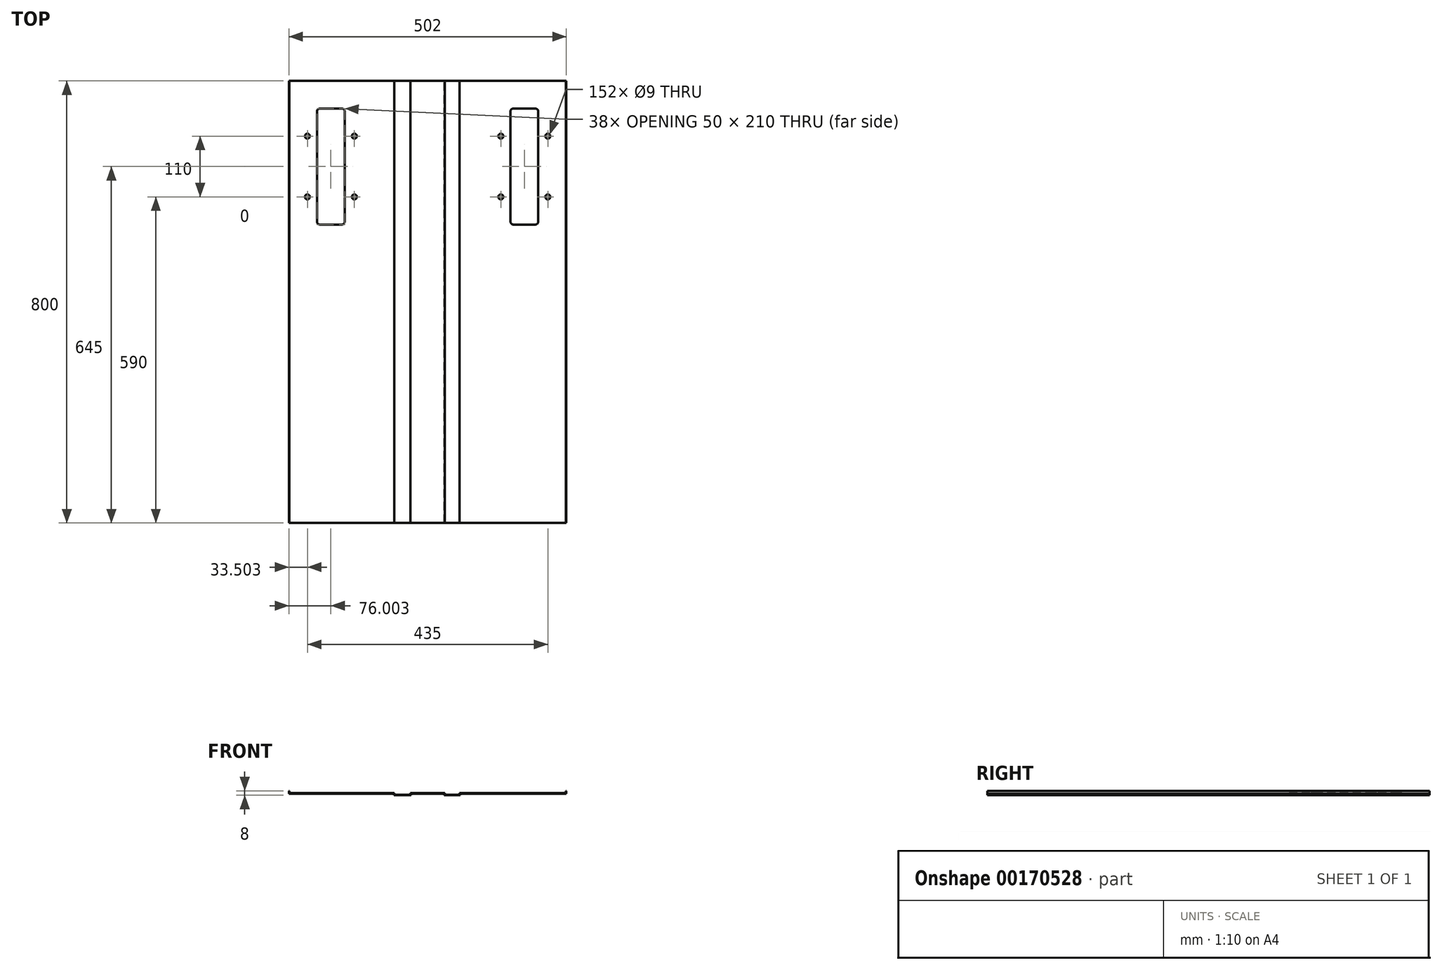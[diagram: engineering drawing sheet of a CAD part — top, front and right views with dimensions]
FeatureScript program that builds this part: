
annotation { "Feature Type Name" : "Feature", "Feature Type Description" : "" }
export const myFeature = defineFeature(function(context is Context, id is Id, definition is map)
    precondition{}
    {
        {
            var Q0;
            Q0=qCreatedBy(makeId("Front.planeOp"),FACE);
            var sketch = newSketch(context, id + "F0", { "sketchPlane" : qUnion([Q0])});
            skLineSegment(sketch, "E0.bottom", {"start": v(-10.98, 0) * mm, "end": v(179.02, 0) * mm});
            skLineSegment(sketch, "E0.top", {"start": v(-9.98, 1) * mm, "end": v(180.02, 1) * mm});
            skLineSegment(sketch, "E0.left", {"start": v(-10.98, 0) * mm, "end": v(-10.98, 1) * mm});
            skLineSegment(sketch, "E0.right", {"start": v(491.02, 0) * mm, "end": v(491.02, 1) * mm});
            skLineSegment(sketch, "E1", {"start": v(240.02, 1) * mm, "end": v(240.02, 44.54) * mm, "construction": true});
            skLineSegment(sketch, "E2.0", {"start": v(179.02, -3) * mm, "end": v(210.02, -3) * mm});
            skLineSegment(sketch, "E3.0", {"start": v(180.02, -2) * mm, "end": v(209.02, -2) * mm});
            skLineSegment(sketch, "E4", {"start": v(210.02, 0) * mm, "end": v(210.02, -3) * mm});
            skLineSegment(sketch, "E5", {"start": v(270.02, 0) * mm, "end": v(270.02, -3) * mm});
            skLineSegment(sketch, "E6.0", {"start": v(180.02, 1) * mm, "end": v(180.02, -2) * mm});
            skLineSegment(sketch, "E7.0", {"start": v(209.02, 1) * mm, "end": v(209.02, -2) * mm});
            skLineSegment(sketch, "E8.0", {"start": v(271.02, 1) * mm, "end": v(271.02, -2) * mm});
            skLineSegment(sketch, "E9.0", {"start": v(298.02, 1) * mm, "end": v(298.02, -2) * mm});
            skLineSegment(sketch, "E10.trimOffspring", {"start": v(271.02, -2) * mm, "end": v(298.02, -2) * mm});
            skLineSegment(sketch, "E11.trimOffspring", {"start": v(270.02, -3) * mm, "end": v(299.02, -3) * mm});
            skLineSegment(sketch, "E12.trimOffspring", {"start": v(179.02, 0) * mm, "end": v(179.02, -3) * mm});
            skLineSegment(sketch, "E13.trimOffspring", {"start": v(210.02, 0) * mm, "end": v(270.02, 0) * mm});
            skLineSegment(sketch, "E14.trimOffspring", {"start": v(209.02, 1) * mm, "end": v(271.02, 1) * mm});
            skPoint(sketch, "E15.orphan", {"position": v(210.02, 16.2) * mm});
            skPoint(sketch, "E16.orphan", {"position": v(270.02, 16.47) * mm});
            skLineSegment(sketch, "E17.trimOffspring", {"start": v(299.02, 0) * mm, "end": v(491.02, 0) * mm});
            skLineSegment(sketch, "E18.trimOffspring", {"start": v(298.02, 1) * mm, "end": v(490.02, 1) * mm});
            skLineSegment(sketch, "E19.trimOffspring", {"start": v(299.02, 0) * mm, "end": v(299.02, -3) * mm});
            skLineSegment(sketch, "E20", {"start": v(-10.98, 1) * mm, "end": v(-10.98, 5) * mm});
            skLineSegment(sketch, "E21", {"start": v(-10.98, 5) * mm, "end": v(-9.98, 5) * mm});
            skLineSegment(sketch, "E22", {"start": v(-9.98, 5) * mm, "end": v(-9.98, 1) * mm});
            skLineSegment(sketch, "E23", {"start": v(491.02, 1) * mm, "end": v(491.02, 5) * mm});
            skLineSegment(sketch, "E24", {"start": v(491.02, 5) * mm, "end": v(490.02, 5) * mm});
            skLineSegment(sketch, "E25", {"start": v(490.02, 5) * mm, "end": v(490.02, 1) * mm});
            skSolve(sketch);
        }
        {
            var Q0;
            Q0 = qSketchRegion(id + "F0", true);
            extrude(context, id + "F1", {"entities" : qUnion([Q0]), "depth" : 800 * mm});
        }
        {
            var Q0;
            Q0=makeQuery(id+"F1.opExtrude","SWEPT_FACE",FACE,{"disambiguationData":[OSD([sQuery(id+"F0.wireOp",EDGE,"E0.top")])]});
            var sketch = newSketch(context, id + "F2", { "sketchPlane" : qUnion([Q0])});
            skLineSegment(sketch, "E26", {"start": v(240.02, 0) * mm, "end": v(240.02, -506.03) * mm, "construction": true});
            skLineSegment(sketch, "E27", {"start": v(440.02, -225) * mm, "end": v(-359.98, -225) * mm, "construction": true});
            skLineSegment(sketch, "E28.bottom", {"start": v(45.02, -50) * mm, "end": v(85.02, -50) * mm});
            skLineSegment(sketch, "E28.top", {"start": v(45.02, -260) * mm, "end": v(85.02, -260) * mm});
            skLineSegment(sketch, "E28.left", {"start": v(90.02, -55) * mm, "end": v(90.02, -255) * mm});
            skLineSegment(sketch, "E28.right", {"start": v(40.02, -55) * mm, "end": v(40.02, -255) * mm});
            skCircle(sketch, "E29", {"center": v(22.52, -100) * mm, "radius": 4.5 * mm});
            skLineSegment(sketch, "E30", {"start": v(90.02, -155) * mm, "end": v(-104.61, -155) * mm, "construction": true});
            skLineSegment(sketch, "E31", {"start": v(65.02, -50) * mm, "end": v(65.02, -176.95) * mm, "construction": true});
            skCircle(sketch, "E32.MirrorC", {"center": v(22.52, -210) * mm, "radius": 4.5 * mm});
            skCircle(sketch, "E33.MirrorC", {"center": v(107.52, -100) * mm, "radius": 4.5 * mm});
            skCircle(sketch, "E34.MirrorC", {"center": v(107.52, -210) * mm, "radius": 4.5 * mm});
            skPoint(sketch, "E35.visualSharp", {"position": v(90.02, -50) * mm});
            skPoint(sketch, "E36.visualSharp", {"position": v(40.02, -50) * mm});
            skPoint(sketch, "E37.visualSharp", {"position": v(90.02, -260) * mm});
            skPoint(sketch, "E38.visualSharp", {"position": v(40.02, -260) * mm});
            skCircle(sketch, "E39.MirrorC", {"center": v(457.52, -210) * mm, "radius": 4.5 * mm});
            skCircle(sketch, "E40.MirrorC", {"center": v(372.52, -100) * mm, "radius": 4.5 * mm});
            skCircle(sketch, "E41.MirrorC", {"center": v(372.52, -210) * mm, "radius": 4.5 * mm});
            skCircle(sketch, "E42.MirrorC", {"center": v(457.52, -100) * mm, "radius": 4.5 * mm});
            skPoint(sketch, "E43.MirrorP", {"position": v(390.02, -260) * mm});
            skLineSegment(sketch, "E44.MirrorCS", {"start": v(435.02, -50) * mm, "end": v(395.02, -50) * mm});
            skLineSegment(sketch, "E45.MirrorCS", {"start": v(435.02, -260) * mm, "end": v(395.02, -260) * mm});
            skPoint(sketch, "E46.MirrorP", {"position": v(440.02, -260) * mm});
            skPoint(sketch, "E47.MirrorP", {"position": v(440.02, -50) * mm});
            skLineSegment(sketch, "E48.MirrorCS", {"start": v(390.02, -55) * mm, "end": v(390.02, -255) * mm});
            skLineSegment(sketch, "E49.MirrorCS", {"start": v(440.02, -55) * mm, "end": v(440.02, -255) * mm});
            skPoint(sketch, "E50.MirrorP", {"position": v(390.02, -50) * mm});
            skLineSegment(sketch, "E51", {"start": v(240.02, 0) * mm, "end": v(240.02, 46.9) * mm, "construction": true});
            skPoint(sketch, "E52.newPointA", {"position": v(40.02, -55) * mm});
            skPoint(sketch, "E52.newPointB", {"position": v(35.02, -50) * mm});
            skArc(sketch, "E52.filletArc", {"start": v(45.02, -50) * mm, "mid": v(41.49, -51.46) * mm, "end": v(40.02, -55) * mm});
            skPoint(sketch, "E53.newPointA", {"position": v(95.02, -50) * mm});
            skPoint(sketch, "E53.newPointB", {"position": v(90.02, -55) * mm});
            skArc(sketch, "E53.filletArc", {"start": v(90.02, -55) * mm, "mid": v(88.56, -51.46) * mm, "end": v(85.02, -50) * mm});
            skPoint(sketch, "E54.newPointA", {"position": v(40.02, -255) * mm});
            skPoint(sketch, "E54.newPointB", {"position": v(35.02, -260) * mm});
            skArc(sketch, "E54.filletArc", {"start": v(40.02, -255) * mm, "mid": v(41.49, -258.54) * mm, "end": v(45.02, -260) * mm});
            skPoint(sketch, "E55.newPointA", {"position": v(90.02, -255) * mm});
            skPoint(sketch, "E55.newPointB", {"position": v(95.02, -260) * mm});
            skArc(sketch, "E55.filletArc", {"start": v(85.02, -260) * mm, "mid": v(88.56, -258.54) * mm, "end": v(90.02, -255) * mm});
            skPoint(sketch, "E56.newPointA", {"position": v(390.02, -255) * mm});
            skPoint(sketch, "E56.newPointB", {"position": v(385.02, -260) * mm});
            skArc(sketch, "E56.filletArc", {"start": v(390.02, -255) * mm, "mid": v(391.49, -258.54) * mm, "end": v(395.02, -260) * mm});
            skPoint(sketch, "E57.newPointA", {"position": v(440.02, -255) * mm});
            skPoint(sketch, "E57.newPointB", {"position": v(445.02, -260) * mm});
            skArc(sketch, "E57.filletArc", {"start": v(435.02, -260) * mm, "mid": v(438.56, -258.54) * mm, "end": v(440.02, -255) * mm});
            skPoint(sketch, "E58.newPointA", {"position": v(390.02, -55) * mm});
            skPoint(sketch, "E58.newPointB", {"position": v(385.02, -50) * mm});
            skArc(sketch, "E58.filletArc", {"start": v(395.02, -50) * mm, "mid": v(391.49, -51.46) * mm, "end": v(390.02, -55) * mm});
            skPoint(sketch, "E59.newPointA", {"position": v(445.02, -50) * mm});
            skPoint(sketch, "E59.newPointB", {"position": v(440.02, -55) * mm});
            skArc(sketch, "E59.filletArc", {"start": v(440.02, -55) * mm, "mid": v(438.56, -51.46) * mm, "end": v(435.02, -50) * mm});
            skSolve(sketch);
        }
        {
            var Q0;
            Q0 = qSketchRegion(id + "F2", true);
            extrude(context, id + "F3", {"entities" : qUnion([Q0]), "operationType" : NewBodyOperationType.REMOVE, "endBound" : BoundingType.THROUGH_ALL, "oppositeDirection" : true, "depth" : 25 * mm});
        }
    });
